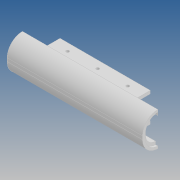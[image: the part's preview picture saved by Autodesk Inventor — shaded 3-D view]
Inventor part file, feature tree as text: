
AUTODESK INVENTOR PART (.ipt)
format: ipt  version: 2020 (Build 240168000, 168)  size: 211,456 bytes
history: native  units: mm
features: extrude x6, sketch x6, other x4, mirror x2, pattern_linear x1, projected_geometry x1
ambient origin geometry x8: Origin, YZ Plane, XZ Plane, XY Plane, X Axis, Y Axis, Z Axis, Center Point
bodies: Body1 (feature_tree)
feature tree (20):
  other  "Твердое тело1"
  extrude  "Выдавливание1"  Depth=180.0mm
  extrude  "Выдавливание2"  Depth=20.0mm
  extrude  "Выдавливание3"  Depth=4.0mm TaperAngle=0.0deg
  pattern_linear  "Прямоуг.массив1"  Spacing1=3.0mm  [1 undecoded]
  extrude  "Выдавливание4"  Depth=180.0mm TaperAngle=0.0deg
  other  "РабПлоскость1"
  extrude  "Выдавливание6"  Depth=4.0mm
  mirror  "Зеркальное отражение4"
  mirror  "Зеркальное отражение2"
  extrude  "Выдавливание5"  Depth=10.0mm
  other  "Толщина1"
  other  "Толщина2"
  sketch  "Эскиз1"
  sketch  "Эскиз2"
  sketch  "Эскиз3"
  sketch  "Эскиз4"
  projected_geometry  "Спроецированная петля1"
  sketch  "Эскиз5"
  sketch  "Эскиз6"
note: 1 required parameter value undecoded (feature->parameter linkage not recoverable at this tier; creation-order binding heuristic only, values carry confidence <= 0.55)
